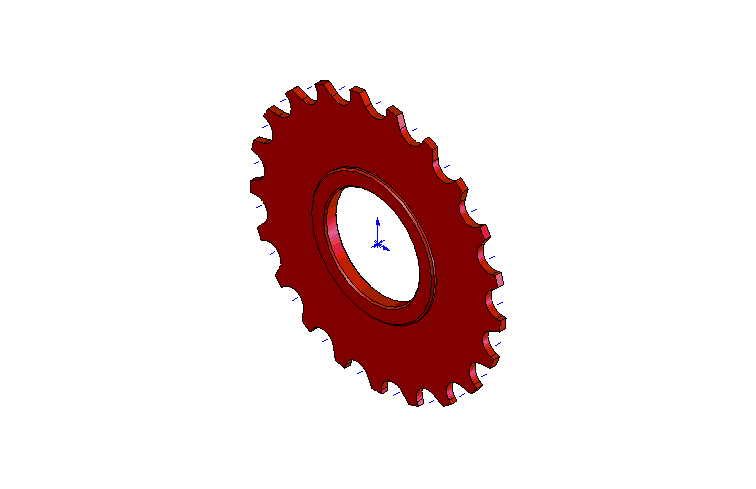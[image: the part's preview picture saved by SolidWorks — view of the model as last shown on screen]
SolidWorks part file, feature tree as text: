
SOLIDWORKS PART (.sldprt)
format: sldprt  version: not decoded by parser v0  size: 242,176 bytes
history: native  units: mm
features: sketch x4, plane x3, extrude x3, material x1, cut_extrude x1, pattern_circular x1, chamfer x1 (+10 scaffold rows collapsed)
feature tree (24):
  scaffold x10  (default folders/planes/origin — collapsed)
  material  "Matériau <non spécifié>"
  plane  "Plan de face"
  plane  "Plan de dessus"
  plane  "Plan de droite"
  sketch  "Esquisse1"  dims[D1=85.5mm]
  extrude  "Extrusion1"  Depth=2mm
  sketch  "Esquisse2"  dims[c1.D1=8.0mm c1.D3=4.0mm c2.D1=8.0mm c2.D3=4.0mm c2.D2=9.5mm c3.D3=4.0mm c3.D2=~2.039916mm c4.D2=35.0deg c4.D3=5.0mm]
  cut_extrude  "Enlèv. mat.-Extru.1"  [1 undecoded]
  pattern_circular  "Répétition circulaire1"  Count=21 Angle=17.142857deg
  sketch  "Esquisse3"  dims[D1=42.0mm]
  extrude  "Extrusion2"  Depth=4.25mm
  sketch  "Esquisse4"  dims[D1=32.0mm]
  extrude  "Enlèv. mat.-Extru.2"  [1 undecoded]
  chamfer  "Chanfrein1"  Distance=0.5mm Angle=45deg
decode coverage: 8 of 10 modeling features carry decoded parameters
note: ~ marks probable driven/reference dimensions
note: 2 parameter values undecoded
note: suppression state not decoded; provenance and decode notes live in map.json
